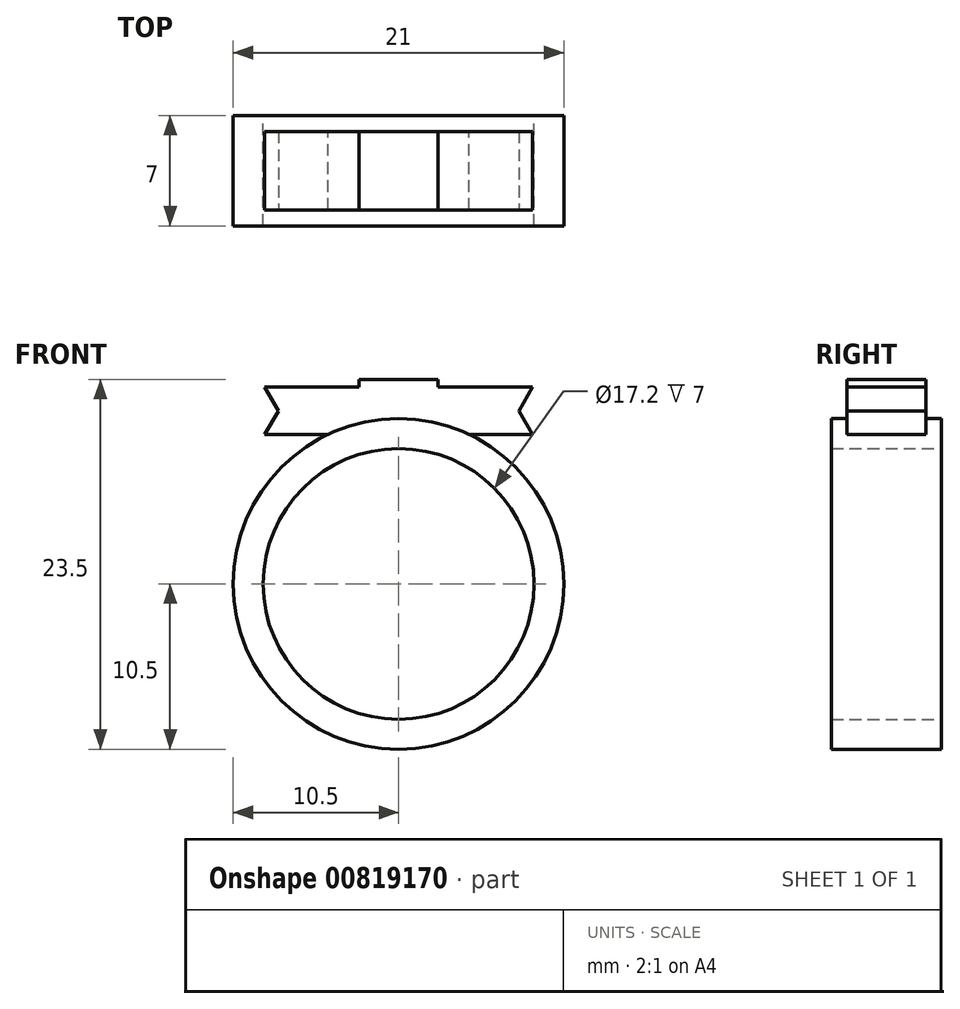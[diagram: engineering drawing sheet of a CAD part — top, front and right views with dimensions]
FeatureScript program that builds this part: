
annotation { "Feature Type Name" : "Feature", "Feature Type Description" : "" }
export const myFeature = defineFeature(function(context is Context, id is Id, definition is map)
    precondition{}
    {
        {
            var Q0;
            Q0=qCreatedBy(makeId("Front.planeOp"),FACE);
            var sketch = newSketch(context, id + "F0", { "sketchPlane" : qUnion([Q0])});
            skCircle(sketch, "E0", {"center": v(0, 0) * mm, "radius": 10.5 * mm});
            skCircle(sketch, "E1", {"center": v(0, 0) * mm, "radius": 8.6 * mm});
            skSolve(sketch);
        }
        {
            var Q0;
            Q0=makeQuery(id+"F0.imprint","IMPRINT",FACE,{"disambiguationData":[TD([[makeQuery(id+"F0.imprint","IMPRINT",EDGE,{"derivedFrom":sQuery(id+"F0.wireOp",EDGE,"E0")}),1.0]])]});
            extrude(context, id + "F1", {"entities" : qUnion([Q0]), "depth" : 7 * mm, "offsetDistance" : 25 * mm});
        }
        {
            var Q0;
            Q0=qCreatedBy(makeId("Top.planeOp"),FACE);
            cPlane(context, id + "F2", {"entities" : qUnion([Q0]), "cplaneType" : CPlaneType.OFFSET, "offset" : 9 * mm, "width" : 150 * mm, "height" : 150 * mm});
        }
        {
            var Q0;
            Q0=qCreatedBy(id+"F2.planeOp",FACE);
            var sketch = newSketch(context, id + "F3", { "sketchPlane" : qUnion([Q0])});
            skLineSegment(sketch, "E2.bottom", {"start": v(-2.5, -1) * mm, "end": v(2.5, -1) * mm});
            skLineSegment(sketch, "E2.top", {"start": v(-2.5, -6) * mm, "end": v(2.5, -6) * mm});
            skLineSegment(sketch, "E2.left", {"start": v(-2.5, -1) * mm, "end": v(-2.5, -6) * mm});
            skLineSegment(sketch, "E2.right", {"start": v(2.5, -1) * mm, "end": v(2.5, -6) * mm});
            skSolve(sketch);
        }
        {
            var Q0;
            Q0 = qSketchRegion(id + "F3", true);
            extrude(context, id + "F4", {"entities" : qUnion([Q0]), "operationType" : NewBodyOperationType.ADD, "depth" : 4 * mm, "offsetDistance" : 25 * mm});
        }
        {
            var Q0;
            Q0=makeQuery(id+"F4.opExtrude","SWEPT_FACE",FACE,{"disambiguationData":[OSD([sQuery(id+"F3.wireOp",EDGE,"E2.right")])]});
            var sketch = newSketch(context, id + "F5", { "sketchPlane" : qUnion([Q0])});
            skLineSegment(sketch, "E3.bottom", {"start": v(-6, 12.5) * mm, "end": v(-1, 12.5) * mm});
            skLineSegment(sketch, "E3.top", {"start": v(-6, 9.5) * mm, "end": v(-1, 9.5) * mm});
            skLineSegment(sketch, "E3.left", {"start": v(-6, 12.5) * mm, "end": v(-6, 9.5) * mm});
            skLineSegment(sketch, "E3.right", {"start": v(-1, 12.5) * mm, "end": v(-1, 9.5) * mm});
            skSolve(sketch);
        }
        {
            var Q0;
            Q0 = qSketchRegion(id + "F5", true);
            extrude(context, id + "F6", {"entities" : qUnion([Q0]), "operationType" : NewBodyOperationType.ADD, "depth" : 6 * mm, "offsetDistance" : 25 * mm});
        }
        {
            var Q0;
            Q0=makeQuery(id+"F6.opExtrude","SWEPT_FACE",FACE,{"disambiguationData":[OSD([sQuery(id+"F5.wireOp",EDGE,"E3.left")])]});
            var sketch = newSketch(context, id + "F7", { "sketchPlane" : qUnion([Q0])});
            skLineSegment(sketch, "E4", {"start": v(8.5, 12.5) * mm, "end": v(7.63, 11) * mm});
            skLineSegment(sketch, "E5", {"start": v(7.63, 11) * mm, "end": v(8.5, 9.5) * mm});
            skLineSegment(sketch, "E6", {"start": v(7.63, 11) * mm, "end": v(8.5, 11) * mm, "construction": true});
            skLineSegment(sketch, "E7", {"start": v(8.5, 12.5) * mm, "end": v(8.5, 9.5) * mm});
            skSolve(sketch);
        }
        {
            var Q0;
            Q0=makeQuery(id+"F7.imprint","IMPRINT",FACE,{"disambiguationData":[TD([[makeQuery(id+"F7.imprint","IMPRINT",EDGE,{"derivedFrom":sQuery(id+"F7.wireOp",EDGE,"E4")}),1.0]])]});
            extrude(context, id + "F8", {"entities" : qUnion([Q0]), "operationType" : NewBodyOperationType.REMOVE, "oppositeDirection" : true, "depth" : 25 * mm, "offsetDistance" : 25 * mm});
        }
        {
            var Q0;
            Q0=makeQuery(id+"F1.opExtrude","SWEPT_BODY",BODY,{"disambiguationData":[OSD([sQuery(id+"F0.wireOp",EDGE,"E0"),sQuery(id+"F0.wireOp",EDGE,"E1")])]});
            var Q1;
            Q1=qCreatedBy(makeId("Right.planeOp"),FACE);
            mirror(context, id + "F9", {"operationType" : NewBodyOperationType.ADD, "entities" : qUnion([Q0]), "mirrorPlane" : qUnion([Q1])});
        }
    });
